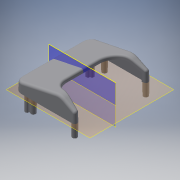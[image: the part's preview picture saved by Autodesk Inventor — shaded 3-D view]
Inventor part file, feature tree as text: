
AUTODESK INVENTOR PART (.ipt)
format: ipt  version: 2016 (Build 200138000, 138)  size: 693,760 bytes
history: native  units: mm
features: extrude x10, sketch x10, projected_geometry x8, fillet x7, reference x3, plane x2, shell x1, mirror x1
ambient origin geometry x8: Origin, YZ Plane, XZ Plane, XY Plane, X Axis, Y Axis, Z Axis, Center Point
bodies: Solid1 (feature_tree)
feature tree (42):
  plane  "Work Plane1"
  extrude  "Extrusion1"  Depth=7.0mm
  fillet  "Fillet1"  Radius=3.0mm
  plane  "Work Plane2"
  extrude  "Extrusion2"  Depth=5.0mm
  fillet  "Fillet2"  Radius=1.0mm
  fillet  "Fillet3"  Radius=1.5mm
  shell  "Shell1"  Thickness=3.05mm
  extrude  "Extrusion3"  Depth=60.0mm
  fillet  "Fillet4"  Radius=1.0mm
  extrude  "Extrusion4"  Depth=3.08mm
  extrude  "Extrusion5"  TaperAngle=15.0deg  [1 undecoded]
  fillet  "Fillet5"  [1 undecoded]
  fillet  "Fillet6"  Radius=10.0mm
  extrude  "Extrusion6"  Depth=5.0mm
  extrude  "Extrusion7"  Depth=0.349066mm TaperAngle=0.0deg
  extrude  "Extrusion8"  Depth=2.0mm
  extrude  "Extrusion9"  Depth=2.0mm
  extrude  "Extrusion11"  Depth=0.174533mm TaperAngle=0.0deg
  mirror  "Mirror3"
  fillet  "Fillet11"  Radius=5.0mm
  sketch  "Sketch1"  dims[d1=1.0mm d2=7.0mm d3=-0.349066mm d4=3.0mm]
  reference  "Reference1"
  sketch  "Sketch2"  dims[d5=60.0mm d6=0.0mm d7=5.0mm d8=1.0mm d9=1.5mm d10=3.05mm]
  sketch  "Sketch3"  dims[d11=3.05mm d12=60.0mm d13=0.174533mm d14=1.0mm]
  projected_geometry  "Projected Loop1"
  sketch  "Sketch4"  dims[d15=3.08mm d16=3.08mm]
  projected_geometry  "Projected Loop2"
  sketch  "Sketch5"  dims[d17=7.0mm d18=-0.087266mm d19=15.0deg d20=15.0deg d21=10.0mm]
  projected_geometry  "Projected Loop3"
  sketch  "Sketch6"  dims[d22=10.0mm d23=0.349066mm d24=5.0mm]
  projected_geometry  "Projected Loop4"
  sketch  "Sketch7"  dims[d25=0.7mm d27=0.0mm d28=0.349066mm]
  projected_geometry  "Projected Loop5"
  sketch  "Sketch8"  dims[d29=5.0mm d30=-0.174533mm d31=2.0mm]
  reference  "Reference2"
  reference  "Reference3"
  sketch  "Sketch9"  dims[d32=16.3mm d33=2.0mm]
  projected_geometry  "Projected Loop6"
  sketch  "Sketch11"  dims[d34=0.0mm d35=0.0mm d36=0.174533mm d37=5.0mm d38=-0.174533mm d54=1.5mm d57=1.5mm d58=10.0mm d59=-0.174533mm d60=0.65mm d61=0.65mm d62=0.65mm d63=0.65mm d64=0.65mm d65=0.65mm d66=0.65mm d67=0.65mm d70=0.4mm]
  projected_geometry  "Projected Loop7"
  projected_geometry  "Projected Loop8"
note: 2 required parameter values undecoded (feature->parameter linkage not recoverable at this tier; creation-order binding heuristic only, values carry confidence <= 0.55)
